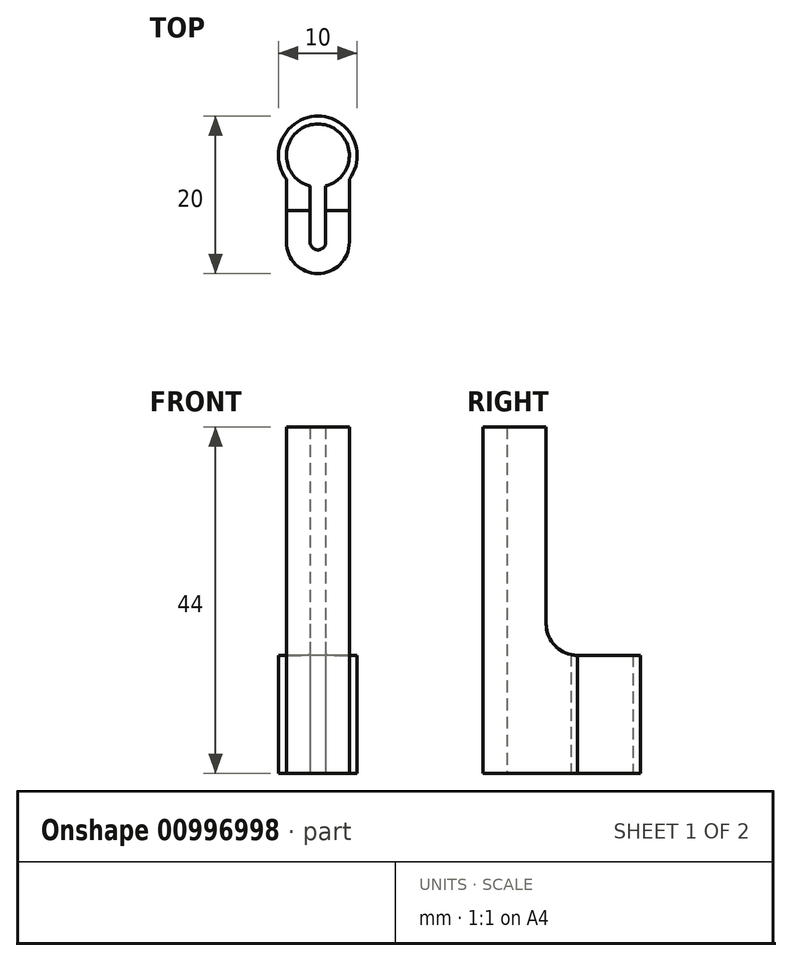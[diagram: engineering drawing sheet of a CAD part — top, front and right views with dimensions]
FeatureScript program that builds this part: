
annotation { "Feature Type Name" : "Feature", "Feature Type Description" : "" }
export const myFeature = defineFeature(function(context is Context, id is Id, definition is map)
    precondition{}
    {
        {
            var Q0;
            Q0=qCreatedBy(makeId("Top.planeOp"),FACE);
            var sketch = newSketch(context, id + "F0", { "sketchPlane" : qUnion([Q0])});
            skCircle(sketch, "E0", {"center": v(0, 0) * mm, "radius": 5 * mm});
            skCircle(sketch, "E1", {"center": v(0, -11) * mm, "radius": 4 * mm});
            skLineSegment(sketch, "E2", {"start": v(-4, -3) * mm, "end": v(-4, -11) * mm});
            skLineSegment(sketch, "E3", {"start": v(4, -3) * mm, "end": v(4, -11) * mm});
            skLineSegment(sketch, "E4", {"start": v(-4, -7) * mm, "end": v(4, -7) * mm});
            skCircle(sketch, "E5", {"center": v(0, -11) * mm, "radius": 1 * mm});
            skLineSegment(sketch, "E6", {"start": v(1, -3.87) * mm, "end": v(1, -11) * mm});
            skLineSegment(sketch, "E7", {"start": v(-1, -3.87) * mm, "end": v(-1, -11) * mm});
            skCircle(sketch, "E8", {"center": v(0, 0) * mm, "radius": 4 * mm});
            skSolve(sketch);
        }
        {
            var Q0;
            {var subQ0=sQuery(id+"F0.wireOp",EDGE,"E0");var subQ1=makeQuery(id+"F0.imprint","INTERSECT",VERTEX,{"derivedFrom":[subQ0,sQuery(id+"F0.wireOp",EDGE,"E2")]});Q0=makeQuery(id+"F0.imprint","IMPRINT",FACE,{"disambiguationData":[TD([[makeQuery(id+"F0.imprint","IMPRINT",EDGE,{"disambiguationData":[TD([[subQ1,-1.0]])],"derivedFrom":subQ0}),1.0]])]});}
            extrude(context, id + "F1", {"entities" : qUnion([Q0]), "depth" : 15 * mm, "offsetDistance" : 25 * mm});
        }
        {
            var Q0;
            {var subQ0=sQuery(id+"F0.wireOp",EDGE,"E2");var subQ1=sQuery(id+"F0.wireOp",EDGE,"E1");var subQ2=makeQuery(id+"F0.imprint","INTERSECT",VERTEX,{"derivedFrom":[subQ1,subQ0]});Q0=makeQuery(id+"F0.imprint","IMPRINT",FACE,{"disambiguationData":[TD([[makeQuery(id+"F0.imprint","IMPRINT",EDGE,{"disambiguationData":[TD([[subQ2,1.0]])],"derivedFrom":subQ1}),-1.0]])]});}
            var Q1;
            {var subQ0=sQuery(id+"F0.wireOp",EDGE,"E3");var subQ1=sQuery(id+"F0.wireOp",EDGE,"E1");var subQ2=makeQuery(id+"F0.imprint","INTERSECT",VERTEX,{"derivedFrom":[subQ1,subQ0]});Q1=makeQuery(id+"F0.imprint","IMPRINT",FACE,{"disambiguationData":[TD([[makeQuery(id+"F0.imprint","IMPRINT",EDGE,{"disambiguationData":[TD([[subQ2,-1.0]])],"derivedFrom":subQ1}),-1.0]])]});}
            var Q2;
            {var subQ0=sQuery(id+"F0.wireOp",EDGE,"E1");var subQ1=makeQuery(id+"F0.imprint","INTERSECT",VERTEX,{"derivedFrom":[subQ0,sQuery(id+"F0.wireOp",EDGE,"E3")]});Q2=makeQuery(id+"F0.imprint","IMPRINT",FACE,{"disambiguationData":[TD([[makeQuery(id+"F0.imprint","IMPRINT",EDGE,{"disambiguationData":[TD([[subQ1,-1.0]])],"derivedFrom":subQ0}),1.0]])]});}
            var Q3;
            {var subQ1=sQuery(id+"F0.wireOp",EDGE,"E2");var subQ5=sQuery(id+"F0.wireOp",EDGE,"E0");var subQ8=makeQuery(id+"F0.imprint","INTERSECT",VERTEX,{"derivedFrom":[subQ5,subQ1]});Q3=makeQuery(id+"F0.imprint","IMPRINT",FACE,{"disambiguationData":[TD([[makeQuery(id+"F0.imprint","IMPRINT",EDGE,{"disambiguationData":[TD([[subQ8,-1.0]])],"derivedFrom":subQ5}),-1.0]])]});}
            var Q4;
            {var subQ0=sQuery(id+"F0.wireOp",EDGE,"E3");var subQ1=sQuery(id+"F0.wireOp",EDGE,"E0");var subQ2=makeQuery(id+"F0.imprint","INTERSECT",VERTEX,{"derivedFrom":[subQ1,subQ0]});Q4=makeQuery(id+"F0.imprint","IMPRINT",FACE,{"disambiguationData":[TD([[makeQuery(id+"F0.imprint","IMPRINT",EDGE,{"disambiguationData":[TD([[subQ2,1.0]])],"derivedFrom":subQ1}),-1.0]])]});}
            extrude(context, id + "F2", {"entities" : qUnion([Q0, Q1, Q2, Q3, Q4]), "operationType" : NewBodyOperationType.ADD, "depth" : 15 * mm, "offsetDistance" : 25 * mm});
        }
        {
            var Q0;
            {var subQ0=sQuery(id+"F0.wireOp",EDGE,"E1");var subQ1=makeQuery(id+"F0.imprint","INTERSECT",VERTEX,{"derivedFrom":[subQ0,sQuery(id+"F0.wireOp",EDGE,"E3")]});Q0=makeQuery(id+"F0.imprint","IMPRINT",FACE,{"disambiguationData":[TD([[makeQuery(id+"F0.imprint","IMPRINT",EDGE,{"disambiguationData":[TD([[subQ1,-1.0]])],"derivedFrom":subQ0}),1.0]])]});}
            var Q1;
            {var subQ0=sQuery(id+"F0.wireOp",EDGE,"E2");var subQ1=sQuery(id+"F0.wireOp",EDGE,"E1");var subQ2=makeQuery(id+"F0.imprint","INTERSECT",VERTEX,{"derivedFrom":[subQ1,subQ0]});Q1=makeQuery(id+"F0.imprint","IMPRINT",FACE,{"disambiguationData":[TD([[makeQuery(id+"F0.imprint","IMPRINT",EDGE,{"disambiguationData":[TD([[subQ2,1.0]])],"derivedFrom":subQ1}),-1.0]])]});}
            var Q2;
            {var subQ0=sQuery(id+"F0.wireOp",EDGE,"E3");var subQ1=sQuery(id+"F0.wireOp",EDGE,"E1");var subQ2=makeQuery(id+"F0.imprint","INTERSECT",VERTEX,{"derivedFrom":[subQ1,subQ0]});Q2=makeQuery(id+"F0.imprint","IMPRINT",FACE,{"disambiguationData":[TD([[makeQuery(id+"F0.imprint","IMPRINT",EDGE,{"disambiguationData":[TD([[subQ2,-1.0]])],"derivedFrom":subQ1}),-1.0]])]});}
            extrude(context, id + "F3", {"entities" : qUnion([Q0, Q1, Q2]), "operationType" : NewBodyOperationType.ADD, "depth" : 44 * mm, "offsetDistance" : 25 * mm});
        }
        {
            var Q0;
            {var subQ0=sQuery(id+"F0.wireOp",EDGE,"E4");var subQ1=sQuery(id+"F0.wireOp",EDGE,"E2");var subQ2=sQuery(id+"F0.wireOp",EDGE,"E7");var subQ3=sQuery(id+"F0.wireOp",EDGE,"E0");Q0=makeQuery(id+"F3.boolean.opBoolean","INTERSECT",EDGE,{"derivedFrom":[makeQuery(id+"F2.boolean.opBoolean","MERGE",FACE,{"derivedFrom":[makeQuery(id+"F1.opExtrude","CAP_FACE",FACE,{"disambiguationData":[OSD([subQ3])],"isStart":false}),makeQuery(id+"F2.opExtrude","CAP_FACE",FACE,{"disambiguationData":[OSD([subQ3,sQuery(id+"F0.wireOp",EDGE,"E1"),subQ1,sQuery(id+"F0.wireOp",EDGE,"E3"),sQuery(id+"F0.wireOp",EDGE,"E5"),sQuery(id+"F0.wireOp",EDGE,"E6"),subQ2])],"isStart":false})]}),makeQuery(id+"F3.opExtrude","SWEPT_FACE",FACE,{"disambiguationData":[OSD([subQ0]),TDD([makeQuery(id+"F0.imprint","IMPRINT",EDGE,{"disambiguationData":[TD([[makeQuery(id+"F0.imprint","INTERSECT",VERTEX,{"derivedFrom":[subQ1,subQ0]}),-1.0]])],"derivedFrom":subQ0})])]})]});}
            var Q1;
            {var subQ0=sQuery(id+"F0.wireOp",EDGE,"E4");var subQ1=sQuery(id+"F0.wireOp",EDGE,"E3");var subQ2=sQuery(id+"F0.wireOp",EDGE,"E6");var subQ3=sQuery(id+"F0.wireOp",EDGE,"E7");var subQ4=sQuery(id+"F0.wireOp",EDGE,"E0");Q1=makeQuery(id+"F3.boolean.opBoolean","INTERSECT",EDGE,{"derivedFrom":[makeQuery(id+"F2.boolean.opBoolean","MERGE",FACE,{"derivedFrom":[makeQuery(id+"F1.opExtrude","CAP_FACE",FACE,{"disambiguationData":[OSD([subQ4,subQ2,subQ3,sQuery(id+"F0.wireOp",EDGE,"E8")])],"isStart":false}),makeQuery(id+"F2.opExtrude","CAP_FACE",FACE,{"disambiguationData":[OSD([subQ4,sQuery(id+"F0.wireOp",EDGE,"E1"),sQuery(id+"F0.wireOp",EDGE,"E2"),subQ1,sQuery(id+"F0.wireOp",EDGE,"E5"),subQ2,subQ3])],"isStart":false})]}),makeQuery(id+"F3.opExtrude","SWEPT_FACE",FACE,{"disambiguationData":[OSD([subQ0]),TDD([makeQuery(id+"F0.imprint","IMPRINT",EDGE,{"disambiguationData":[TD([[makeQuery(id+"F0.imprint","INTERSECT",VERTEX,{"derivedFrom":[subQ1,subQ0]}),1.0]])],"derivedFrom":subQ0})])]})]});}
            fillet(context, id + "F4", {"entities" : qUnion([Q0, Q1]), "radius" : 4 * mm, "tangentPropagation" : true, "allowEdgeOverflow" : false});
        }
    });
